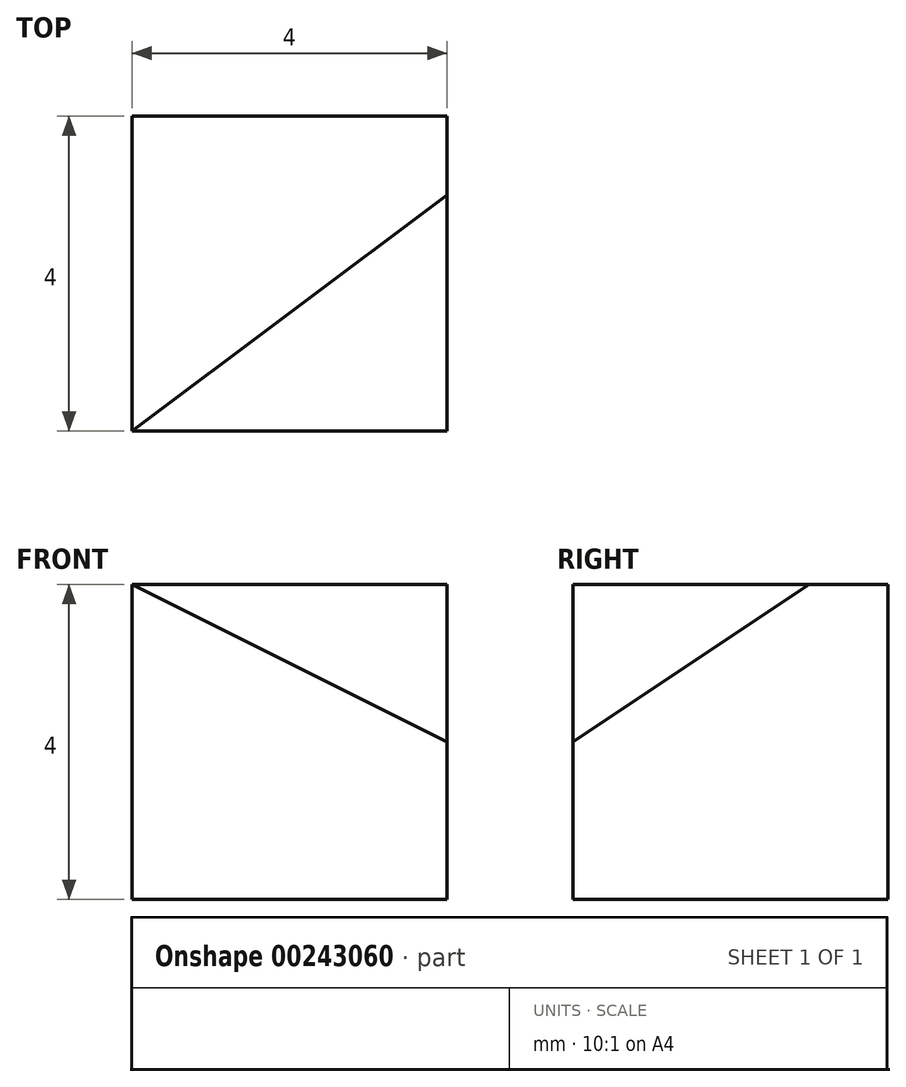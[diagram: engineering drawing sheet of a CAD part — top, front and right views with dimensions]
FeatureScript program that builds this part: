
annotation { "Feature Type Name" : "Feature", "Feature Type Description" : "" }
export const myFeature = defineFeature(function(context is Context, id is Id, definition is map)
    precondition{}
    {
        {
            var Q0;
            Q0=qCreatedBy(makeId("Front.planeOp"),FACE);
            var sketch = newSketch(context, id + "F0", { "sketchPlane" : qUnion([Q0])});
            skLineSegment(sketch, "E0.bottom", {"start": v(0, 0) * mm, "end": v(4, 0) * mm});
            skLineSegment(sketch, "E0.top", {"start": v(0, 4) * mm, "end": v(4, 4) * mm});
            skLineSegment(sketch, "E0.left", {"start": v(0, 0) * mm, "end": v(0, 4) * mm});
            skLineSegment(sketch, "E0.right", {"start": v(4, 0) * mm, "end": v(4, 4) * mm});
            skLineSegment(sketch, "E1", {"start": v(0, 4) * mm, "end": v(4, 2) * mm});
            skSolve(sketch);
        }
        {
            var Q0;
            Q0 = qSketchRegion(id + "F0", true);
            extrude(context, id + "F1", {"entities" : qUnion([Q0]), "oppositeDirection" : true, "depth" : 4 * mm});
        }
        {
            var Q0;
            Q0=qCreatedBy(makeId("Front.planeOp"),FACE);
            var sketch = newSketch(context, id + "F2", { "sketchPlane" : qUnion([Q0])});
            skPoint(sketch, "E2.0", {"position": v(0, 4) * mm});
            skPoint(sketch, "E3.0", {"position": v(4, 2) * mm});
            skLineSegment(sketch, "E4", {"start": v(0, 4) * mm, "end": v(4, 2) * mm});
            skPoint(sketch, "E5.0", {"position": v(4, 4) * mm});
            skSolve(sketch);
        }
        {
            var Q0;
            Q0=makeQuery(id+"F1.opExtrude","SWEPT_FACE",FACE,{"disambiguationData":[OSD([sQuery(id+"F0.wireOp",EDGE,"E0.right")])]});
            var sketch = newSketch(context, id + "F3", { "sketchPlane" : qUnion([Q0])});
            skLineSegment(sketch, "E6", {"start": v(0, 2) * mm, "end": v(3, 4) * mm});
            skSolve(sketch);
        }
        {
            var Q0;
            Q0=sQuery(id+"F3.wireOp",VERTEX,"E6.end");
            var Q1;
            Q1=sQuery(id+"F2.wireOp",VERTEX,"E3.0");
            var Q2;
            Q2=sQuery(id+"F2.wireOp",VERTEX,"E2.0");
            cPlane(context, id + "F4", {"entities" : qUnion([Q0, Q1, Q2]), "cplaneType" : CPlaneType.THREE_POINT, "offset" : 25 * mm, "width" : 150 * mm, "height" : 150 * mm});
        }
        {
            var Q0;
            Q0=qCreatedBy(id+"F4.planeOp",FACE);
            var sketch = newSketch(context, id + "F5", { "sketchPlane" : qUnion([Q0])});
            skPoint(sketch, "E7.0", {"position": v(3.05, 4.71) * mm});
            skPoint(sketch, "E8.0", {"position": v(3.05, 1.1) * mm});
            skPoint(sketch, "E9.0", {"position": v(-1.28, 2.22) * mm});
            skLineSegment(sketch, "E10", {"start": v(3.05, 4.71) * mm, "end": v(3.05, 1.1) * mm});
            skLineSegment(sketch, "E11", {"start": v(3.05, 4.71) * mm, "end": v(-1.28, 2.22) * mm});
            skLineSegment(sketch, "E12", {"start": v(-1.28, 2.22) * mm, "end": v(3.05, 1.1) * mm});
            skSolve(sketch);
        }
        {
            var Q0;
            Q0 = qSketchRegion(id + "F5", true);
            extrude(context, id + "F6", {"entities" : qUnion([Q0]), "operationType" : NewBodyOperationType.REMOVE, "depth" : 25 * mm});
        }
    });
